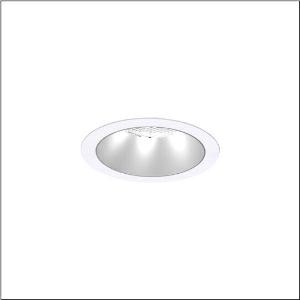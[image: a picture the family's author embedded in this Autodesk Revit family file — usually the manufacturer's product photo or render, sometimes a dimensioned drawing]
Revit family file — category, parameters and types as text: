
# Revit family: lunis_21_l_51db19td91c
name_source: partatom
category: Lighting Fixtures
units: mm (PartAtom-declared; Revit-internal decimal feet)

## family parameters
Cut with Voids When Loaded = No
Host = Face
Light Source = No
Part Type = Normal
Room Calculation Point = No
Round Connector Dimension = Use Diameter
Shared = No

## types (1)
- --- (1 x LED, 3900 lm, 25.4 W, 4000K)
    Apparent Load = 25 VA
    CIE Flux Codes = 90 99 100 100 100
    Color Rendering = 80
    Color Temperature = 4000K
    Default Elevation = 1800 mm
    Description = Lunis 21,  L, downlight, light control with lens, of PMMA, anti glare with reflector, of aluminium, matt, light emission: direct distribution, LED rated luminous flux: 2.020lm, light colour: 8tw, with terminal, 5-pole, mains connection: 220..240V, AC/DC, 0/50..60Hz, housing, round, of diecast aluminium, traffic white (RAL 9016), diameter: 165mm, clamping range: 1..40mm, protection rating (complete): IP20, protection rating (on room side): IP54, insulation class (complete): insulation class II (safety insulation), certification: CE, impact resistance: IK03, packaging unit: 1 piece
    Height = 0 mm  [stored 0 ft]
    Lamp = 1 x LED
    Lamp Light Flux = 3900 lm
    Lamp Power = 25.4 W
    Lamp count = 1
    Length = 165 mm
    Luminous efficacy = 154 lm/W
    Manufacturer = Siteco
    ModVariant = No
    Model = 51DB19TD91C
    Mounting Place = Ceiling
    Mounting Type = Recessed
    Number of Poles = 1
    OnlyDefault = Yes
    Power Factor = 1
    Product Name = Lunis 21 L
    Product group = downlight
    ProductGroupID = 401
    Protection Class = Protection class II
    Protection Degree = IP 20
    RLX_Detail_Level = 1
    RLX_Emergency_Light_Flux = 0 lm
    RLX_Emergency_Type = 0
    RLX_Emergency_Type_DB = No
    RlxData = <blob elided: 15129 chars, md5=2385ab94>
    Socket = socket
    Standby Power = 0 W
    System Light Flux = 3900 lm
    System Power = 25 W
    Type Comments = individual setting: colour temperature 4000K, luminous flux: 100 % | (ON | ON | OFF | OFF) | 700 mA
    Type Image = l_1291096.jpg
    URL = http://relux.com
    VarID = @adj_031445
    Voltage = 0 V
    Weight = 0.00 kg
    Width = 0 mm  [stored 0 ft]

note: [stored X ft] marks values corroborated as IEEE doubles in the binary element streams (Revit-internal decimal feet)

## geometry (parser evidence)
native form markers: Sweep x11
no freeform markers — native parametric forms only
